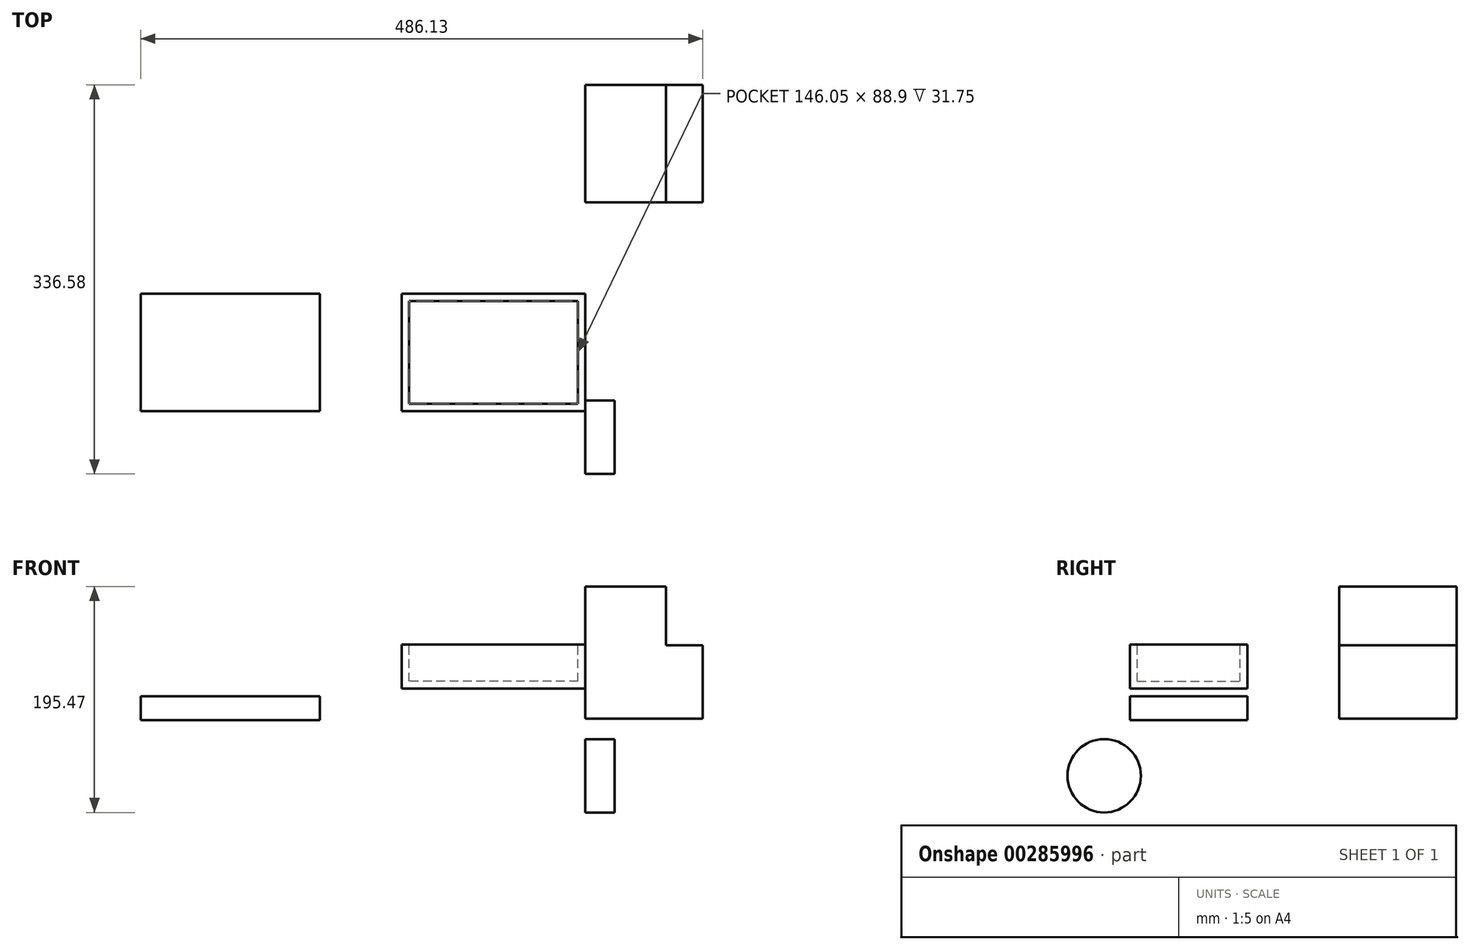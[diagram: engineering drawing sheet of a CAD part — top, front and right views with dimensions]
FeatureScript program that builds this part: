
annotation { "Feature Type Name" : "Feature", "Feature Type Description" : "" }
export const myFeature = defineFeature(function(context is Context, id is Id, definition is map)
    precondition{}
    {
        {
            var Q0;
            Q0=qCreatedBy(makeId("Right.planeOp"),FACE);
            var sketch = newSketch(context, id + "F0", { "sketchPlane" : qUnion([Q0])});
            skLineSegment(sketch, "E0.bottom", {"start": v(79.18, -279.98) * mm, "end": v(180.78, -279.98) * mm});
            skLineSegment(sketch, "E0.top", {"start": v(79.18, -343.48) * mm, "end": v(180.78, -343.48) * mm});
            skLineSegment(sketch, "E0.left", {"start": v(79.18, -279.98) * mm, "end": v(79.18, -343.48) * mm});
            skLineSegment(sketch, "E0.right", {"start": v(180.78, -279.98) * mm, "end": v(180.78, -343.48) * mm});
            skLineSegment(sketch, "E1.top", {"start": v(79.18, -229.18) * mm, "end": v(180.78, -229.18) * mm});
            skLineSegment(sketch, "E1.left", {"start": v(79.18, -279.98) * mm, "end": v(79.18, -229.18) * mm});
            skLineSegment(sketch, "E1.right", {"start": v(180.78, -279.98) * mm, "end": v(180.78, -229.18) * mm});
            skSolve(sketch);
        }
        {
            var Q0;
            Q0=makeQuery(id+"F0.imprint","IMPRINT",FACE,{"disambiguationData":[TD([[makeQuery(id+"F0.imprint","IMPRINT",EDGE,{"derivedFrom":sQuery(id+"F0.wireOp",EDGE,"E0.top")}),1.0]])]});
            extrude(context, id + "F1", {"entities" : qUnion([Q0]), "depth" : 101.6 * mm});
        }
        {
            var Q0;
            Q0 = qSketchRegion(id + "F0", true);
            extrude(context, id + "F2", {"entities" : qUnion([Q0]), "operationType" : NewBodyOperationType.ADD, "depth" : 69.85 * mm});
        }
        {
            var Q0;
            Q0=qCreatedBy(makeId("Front.planeOp"),FACE);
            var sketch = newSketch(context, id + "F3", { "sketchPlane" : qUnion([Q0])});
            skLineSegment(sketch, "E2.top", {"start": v(0, -317.54) * mm, "end": v(-158.75, -317.54) * mm});
            skLineSegment(sketch, "E3.bottom", {"start": v(-158.75, -317.54) * mm, "end": v(0, -317.54) * mm});
            skLineSegment(sketch, "E3.top", {"start": v(-158.75, -279.44) * mm, "end": v(0, -279.44) * mm});
            skLineSegment(sketch, "E3.left", {"start": v(-158.75, -317.54) * mm, "end": v(-158.75, -279.44) * mm});
            skLineSegment(sketch, "E3.right", {"start": v(0, -317.54) * mm, "end": v(0, -279.44) * mm});
            skLineSegment(sketch, "E4.bottom", {"start": v(-229.73, -324.22) * mm, "end": v(-384.53, -324.22) * mm});
            skLineSegment(sketch, "E4.top", {"start": v(-229.73, -344.79) * mm, "end": v(-384.53, -344.79) * mm});
            skLineSegment(sketch, "E4.left", {"start": v(-229.73, -324.22) * mm, "end": v(-229.73, -344.79) * mm});
            skLineSegment(sketch, "E4.right", {"start": v(-384.53, -324.22) * mm, "end": v(-384.53, -344.79) * mm});
            skSolve(sketch);
        }
        {
            var Q0;
            Q0 = qSketchRegion(id + "F3", true);
            extrude(context, id + "F4", {"entities" : qUnion([Q0]), "depth" : 101.6 * mm});
        }
        {
            var Q0;
            Q0=qCreatedBy(makeId("Right.planeOp"),FACE);
            var sketch = newSketch(context, id + "F5", { "sketchPlane" : qUnion([Q0])});
            skCircle(sketch, "E5", {"center": v(-124.05, -392.9) * mm, "radius": 31.75 * mm});
            skSolve(sketch);
        }
        {
            var Q0;
            Q0=makeQuery(id+"F5.imprint","IMPRINT",FACE,{"disambiguationData":[TD([[makeQuery(id+"F5.imprint","IMPRINT",EDGE,{"derivedFrom":sQuery(id+"F5.wireOp",EDGE,"E5")}),1.0]])]});
            extrude(context, id + "F6", {"entities" : qUnion([Q0]), "depth" : 25.4 * mm});
        }
        {
            var Q0;
            Q0=makeQuery(id+"F4.opExtrude","SWEPT_FACE",FACE,{"disambiguationData":[OSD([sQuery(id+"F3.wireOp",EDGE,"E3.top")])]});
            shell(context, id + "F7", {"entities" : qUnion([Q0]), "thickness" : 6.35 * mm});
        }
    });
